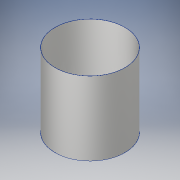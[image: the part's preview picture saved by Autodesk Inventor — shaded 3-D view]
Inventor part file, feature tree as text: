
AUTODESK INVENTOR PART (.ipt)
format: ipt  version: 2018 (Build 220112000, 112)  size: 101,888 bytes
history: native  units: in
note: dims shown in document units (in); Inventor stores cm internally (conversion verified against a paired STEP export)
features: extrude x1, sketch x1
ambient origin geometry x8: Origin, YZ Plane, XZ Plane, XY Plane, X Axis, Y Axis, Z Axis, Center Point
bodies: Solid1 (feature_tree)
feature tree (2):
  extrude  "Extrusion1"  Depth=19.0in
  sketch  "Sketch1"  dims[d0=18.0in d1=18.065in d2=19.0in d3=0.0in]
